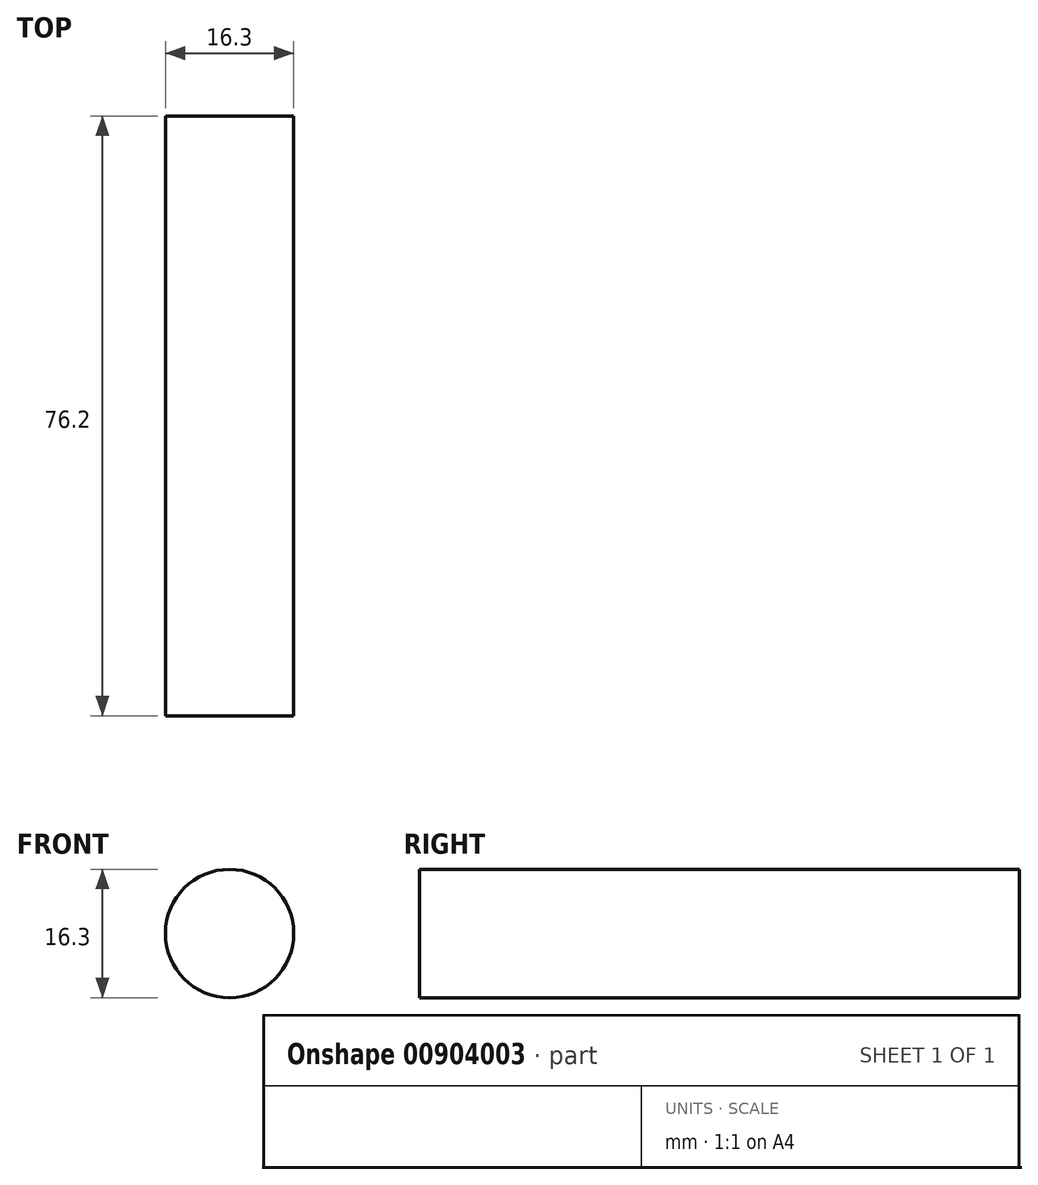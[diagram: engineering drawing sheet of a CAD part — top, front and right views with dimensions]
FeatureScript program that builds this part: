
annotation { "Feature Type Name" : "Feature", "Feature Type Description" : "" }
export const myFeature = defineFeature(function(context is Context, id is Id, definition is map)
    precondition{}
    {
        {
            var Q0;
            Q0=qCreatedBy(makeId("Front.planeOp"),FACE);
            var sketch = newSketch(context, id + "F0", { "sketchPlane" : qUnion([Q0])});
            skCircle(sketch, "E0", {"center": v(0, 0) * mm, "radius": 8.15 * mm});
            skSolve(sketch);
        }
        {
            var Q0;
            Q0=makeQuery(id+"F0.imprint","IMPRINT",FACE,{"disambiguationData":[TD([[makeQuery(id+"F0.imprint","IMPRINT",EDGE,{"derivedFrom":sQuery(id+"F0.wireOp",EDGE,"E0")}),1.0]])]});
            extrude(context, id + "F1", {"entities" : qUnion([Q0]), "depth" : 76.2 * mm, "offsetDistance" : 25.4 * mm});
        }
    });
